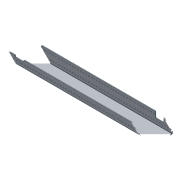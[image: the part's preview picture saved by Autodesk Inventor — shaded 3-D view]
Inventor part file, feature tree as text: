
AUTODESK INVENTOR PART (.ipt)
format: ipt  version: 2016 (Build 200138000, 138)  size: 422,400 bytes
history: native  units: in
note: dims shown in document units (in); Inventor stores cm internally (conversion verified against a paired STEP export)
features: extrude x1, fillet x1, sketch x1, other x1
ambient origin geometry x8: Origin, YZ Plane, XZ Plane, XY Plane, X Axis, Y Axis, Z Axis, Center Point
bodies: Solid1 (feature_tree)
feature tree (4):
  extrude  "Extrusion2"  Depth=0.125in
  fillet  "Fillet2"  Radius=0.2in
  sketch  "Sketch2"  dims[d7=0.2in d8=0.2in d9=0.2in d10=0.2in d11=0.3in d12=0.3in d13=5.0in d14=0.0in d15=0.125in]
  other  "_AM14U3 End Sheet Rev1_-_LPattern4_"
